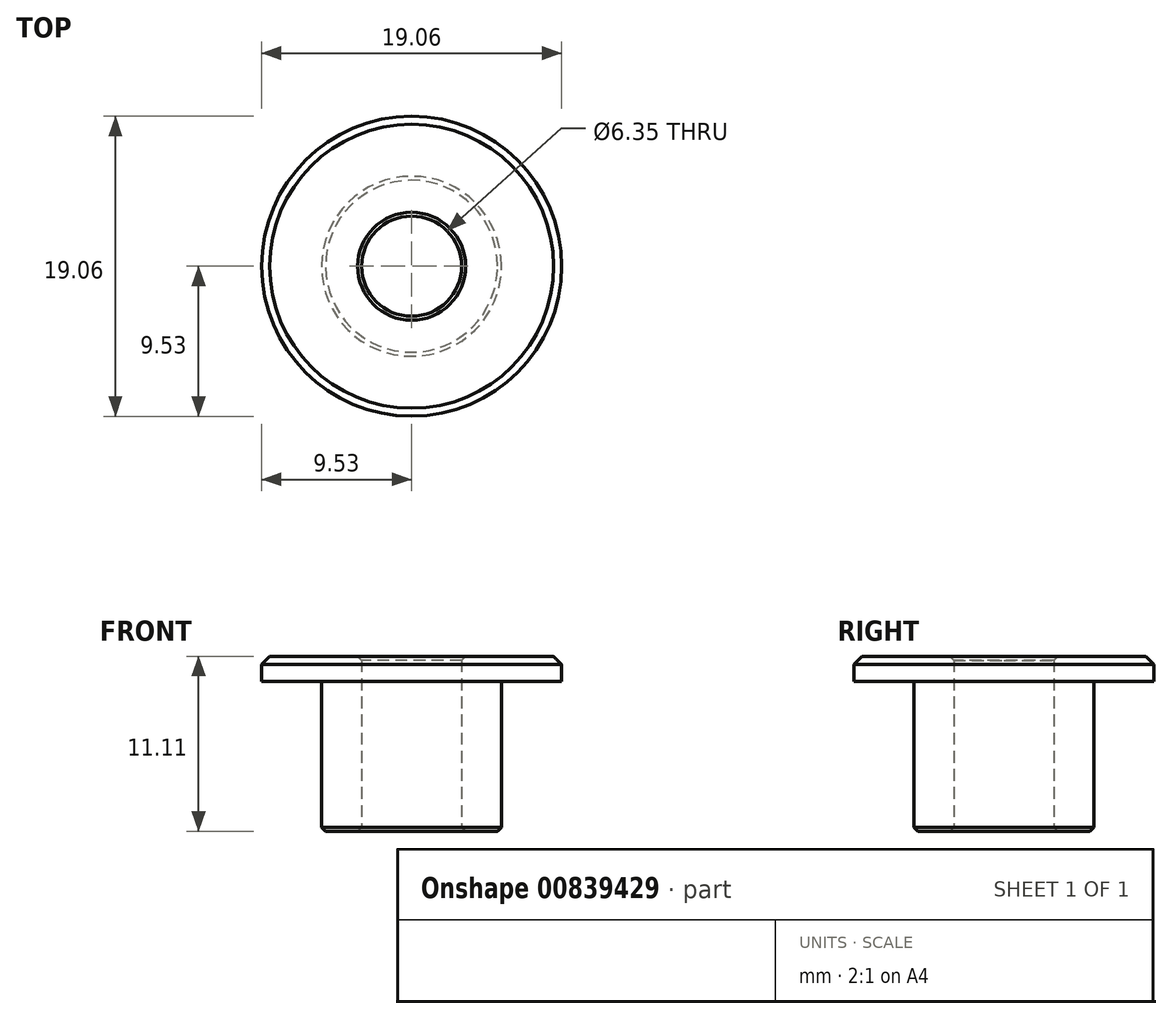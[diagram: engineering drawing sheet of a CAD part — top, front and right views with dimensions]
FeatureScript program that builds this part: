
annotation { "Feature Type Name" : "Feature", "Feature Type Description" : "" }
export const myFeature = defineFeature(function(context is Context, id is Id, definition is map)
    precondition{}
    {
        {
            var Q0;
            Q0=qCreatedBy(makeId("Top.planeOp"),FACE);
            var sketch = newSketch(context, id + "F0", { "sketchPlane" : qUnion([Q0])});
            skCircle(sketch, "E0", {"center": v(0, 0) * mm, "radius": 5.72 * mm});
            skCircle(sketch, "E1", {"center": v(0, 0) * mm, "radius": 3.18 * mm});
            skSolve(sketch);
        }
        {
            var Q0;
            Q0 = qSketchRegion(id + "F0", true);
            extrude(context, id + "F1", {"entities" : qUnion([Q0]), "depth" : 9.52 * mm, "offsetDistance" : 25.4 * mm});
        }
        {
            var Q0;
            Q0=makeQuery(id+"F1.opExtrude","CAP_FACE",FACE,{"disambiguationData":[OSD([sQuery(id+"F0.wireOp",EDGE,"E0"),sQuery(id+"F0.wireOp",EDGE,"E1")])],"isStart":false});
            var sketch = newSketch(context, id + "F2", { "sketchPlane" : qUnion([Q0])});
            skCircle(sketch, "E2", {"center": v(0, 0) * mm, "radius": 9.53 * mm});
            skSolve(sketch);
        }
        {
            var Q0;
            Q0=makeQuery(id+"F2.imprint","IMPRINT",FACE,{"disambiguationData":[TD([[makeQuery(id+"F2.imprint","IMPRINT",EDGE,{"derivedFrom":sQuery(id+"F2.wireOp",EDGE,"E2")}),1.0]])]});
            var Q1;
            Q1=makeQuery(id+"F2.imprint","IMPRINT",FACE,{"disambiguationData":[TD([[makeQuery(id+"F2.imprint","IMPRINT",EDGE,{"derivedFrom":makeQuery(id+"F1.opExtrude","CAP_EDGE",EDGE,{"disambiguationData":[OSD([sQuery(id+"F0.wireOp",EDGE,"E0")])],"isStart":false})}),1.0]])]});
            extrude(context, id + "F3", {"entities" : qUnion([Q0, Q1]), "operationType" : NewBodyOperationType.ADD, "depth" : 1.59 * mm, "offsetDistance" : 25.4 * mm});
        }
        {
            var Q0;
            Q0=makeQuery(id+"F3.opExtrude","CAP_EDGE",EDGE,{"disambiguationData":[OSD([sQuery(id+"F2.wireOp",EDGE,"E2")])],"isStart":false});
            chamfer(context, id + "F4", {"entities" : qUnion([Q0]), "width" : 0.5 * mm, "tangentPropagation" : true});
        }
        {
            var Q0;
            Q0=makeQuery(id+"F3.opExtrude","CAP_EDGE",EDGE,{"disambiguationData":[OSD([sQuery(id+"F0.wireOp",EDGE,"E1")])],"isStart":false});
            var Q1;
            Q1=makeQuery(id+"F1.opExtrude","CAP_EDGE",EDGE,{"disambiguationData":[OSD([sQuery(id+"F0.wireOp",EDGE,"E0")])],"isStart":true});
            var Q2;
            Q2=makeQuery(id+"F1.opExtrude","CAP_EDGE",EDGE,{"disambiguationData":[OSD([sQuery(id+"F0.wireOp",EDGE,"E1")])],"isStart":true});
            chamfer(context, id + "F5", {"entities" : qUnion([Q0, Q1, Q2]), "width" : 0.25 * mm, "tangentPropagation" : true});
        }
    });
